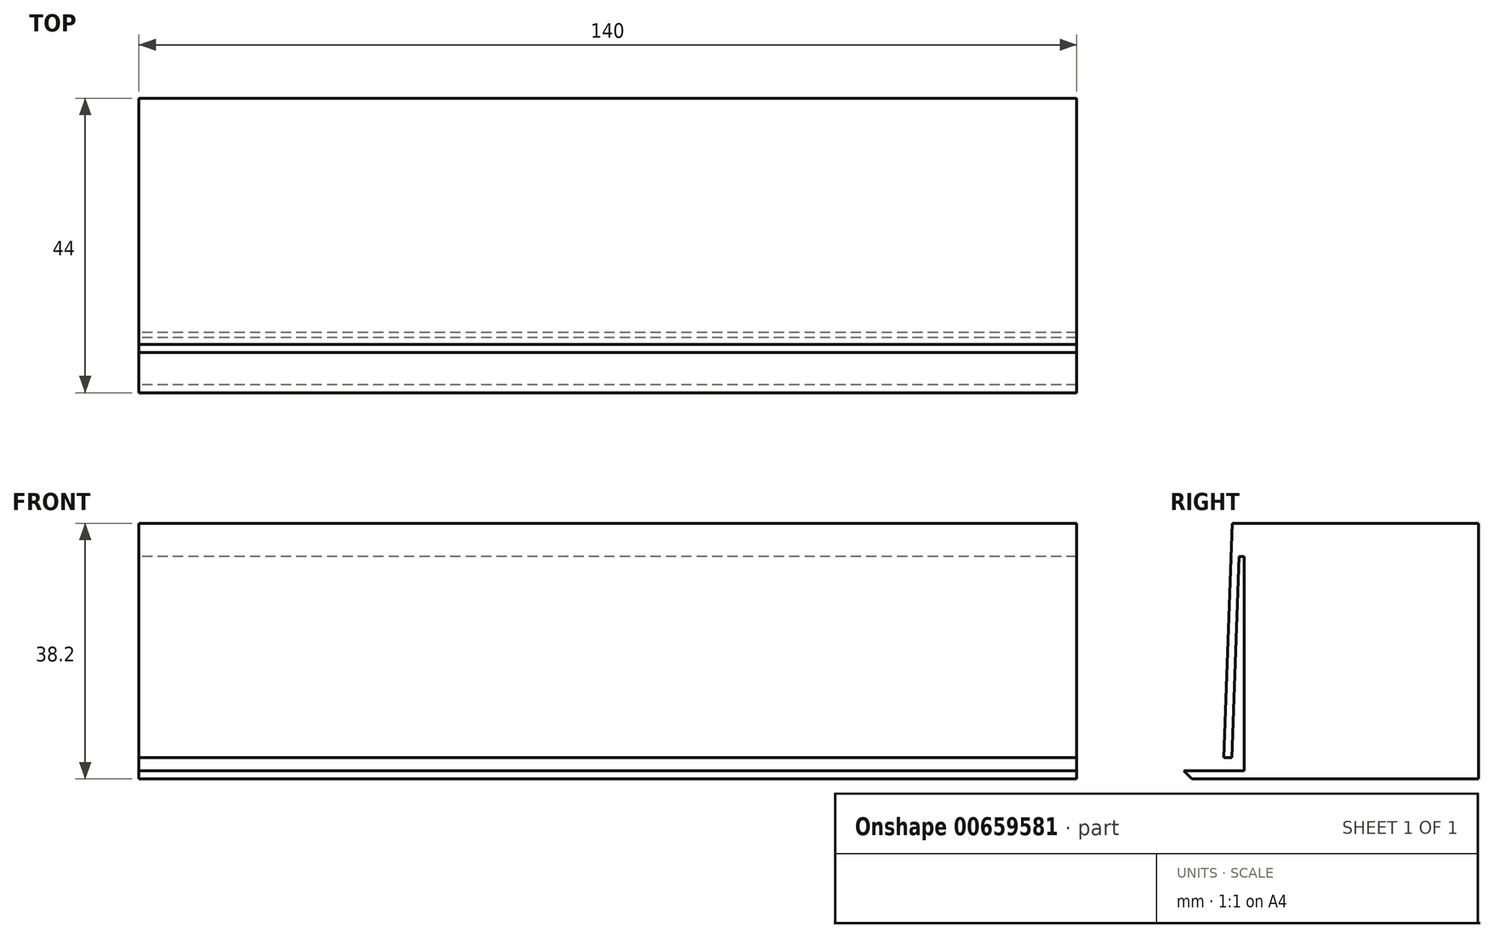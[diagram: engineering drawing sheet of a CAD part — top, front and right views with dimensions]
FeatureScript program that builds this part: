
annotation { "Feature Type Name" : "Feature", "Feature Type Description" : "" }
export const myFeature = defineFeature(function(context is Context, id is Id, definition is map)
    precondition{}
    {
        {
            var Q0;
            Q0=qCreatedBy(makeId("Right.planeOp"),FACE);
            var sketch = newSketch(context, id + "F0", { "sketchPlane" : qUnion([Q0])});
            skLineSegment(sketch, "E0.bottom", {"start": v(0, 0) * mm, "end": v(38, 0) * mm});
            skLineSegment(sketch, "E0.top", {"start": v(0, 37) * mm, "end": v(38, 37) * mm, "construction": true});
            skLineSegment(sketch, "E0.left", {"start": v(0, 0) * mm, "end": v(0, 37) * mm, "construction": true});
            skLineSegment(sketch, "E0.right", {"start": v(38, 0) * mm, "end": v(38, 37) * mm});
            skLineSegment(sketch, "E1", {"start": v(0, 2) * mm, "end": v(1.22, 37) * mm});
            skLineSegment(sketch, "E2", {"start": v(1.22, 37) * mm, "end": v(2.42, 37) * mm});
            skLineSegment(sketch, "E3", {"start": v(2.42, 37) * mm, "end": v(1.2, 2) * mm});
            skLineSegment(sketch, "E4", {"start": v(1.2, 2) * mm, "end": v(0, 2) * mm});
            skLineSegment(sketch, "E5", {"start": v(3, 53.55) * mm, "end": v(3, 0) * mm});
            skLineSegment(sketch, "E6", {"start": v(2.42, 37) * mm, "end": v(38, 37) * mm});
            skLineSegment(sketch, "E7.bottom", {"start": v(38, 0) * mm, "end": v(-6, 0) * mm});
            skLineSegment(sketch, "E7.top", {"start": v(38, -1.2) * mm, "end": v(-4.8, -1.2) * mm});
            skLineSegment(sketch, "E7.left", {"start": v(38, 0) * mm, "end": v(38, -1.2) * mm});
            skLineSegment(sketch, "E7.right", {"start": v(-6, 0) * mm, "end": v(-4.8, -1.2) * mm});
            skPoint(sketch, "E8", {"position": v(3, 37) * mm});
            skLineSegment(sketch, "E9", {"start": v(3, 32) * mm, "end": v(2.25, 32) * mm});
            skSolve(sketch);
        }
        {
            var Q0;
            Q0 = qSketchRegion(id + "F0", true);
            extrude(context, id + "F1", {"entities" : qUnion([Q0]), "depth" : 140 * mm, "offsetDistance" : 25 * mm});
        }
    });
